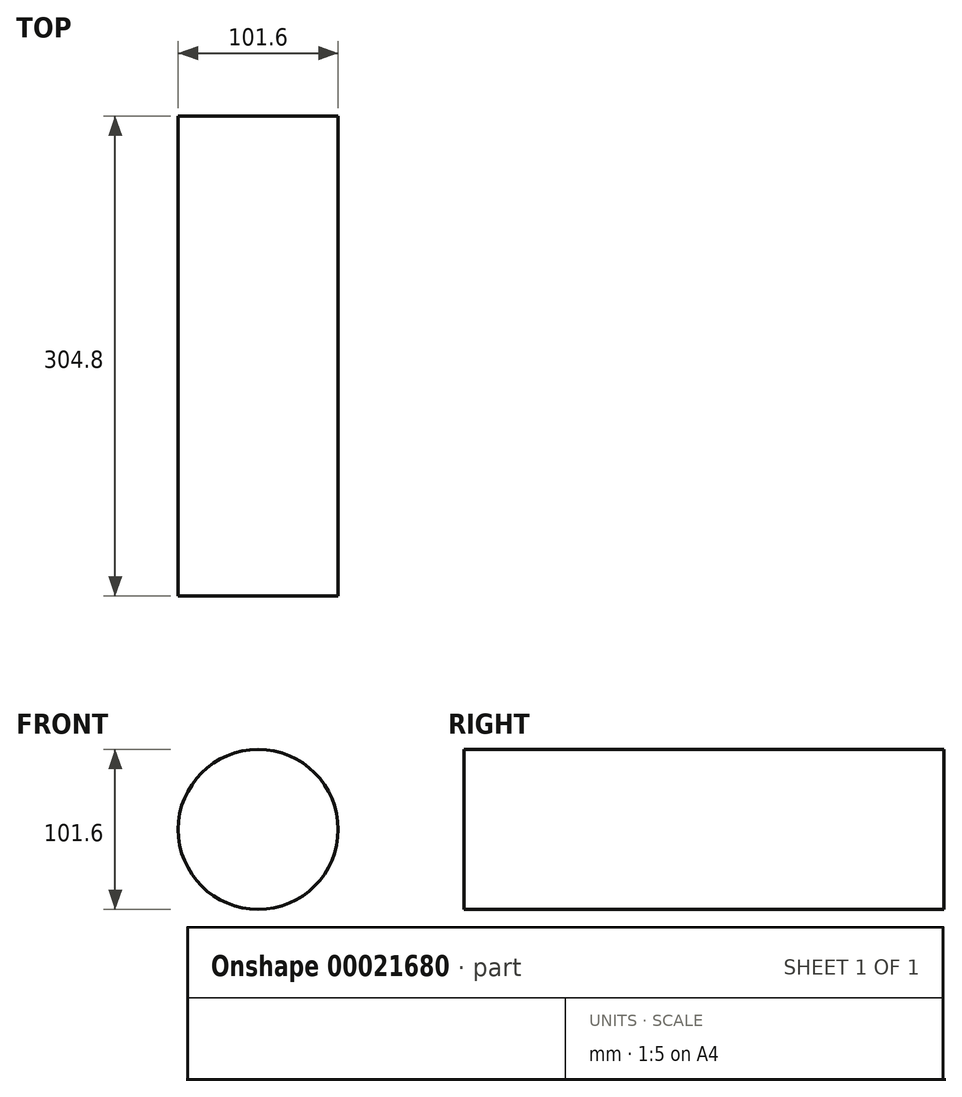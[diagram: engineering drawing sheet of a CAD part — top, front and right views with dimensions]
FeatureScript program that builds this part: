
annotation { "Feature Type Name" : "Feature", "Feature Type Description" : "" }
export const myFeature = defineFeature(function(context is Context, id is Id, definition is map)
    precondition{}
    {
        {
            var Q0;
            Q0=qCreatedBy(makeId("Front.planeOp"),FACE);
            var sketch = newSketch(context, id + "F0", { "sketchPlane" : qUnion([Q0])});
            skCircle(sketch, "E0", {"center": v(0, 0) * mm, "radius": 50.8 * mm});
            skSolve(sketch);
        }
        {
            var Q0;
            Q0 = qSketchRegion(id + "F0", true);
            extrude(context, id + "F1", {"entities" : qUnion([Q0]), "depth" : 304.8 * mm});
        }
    });
